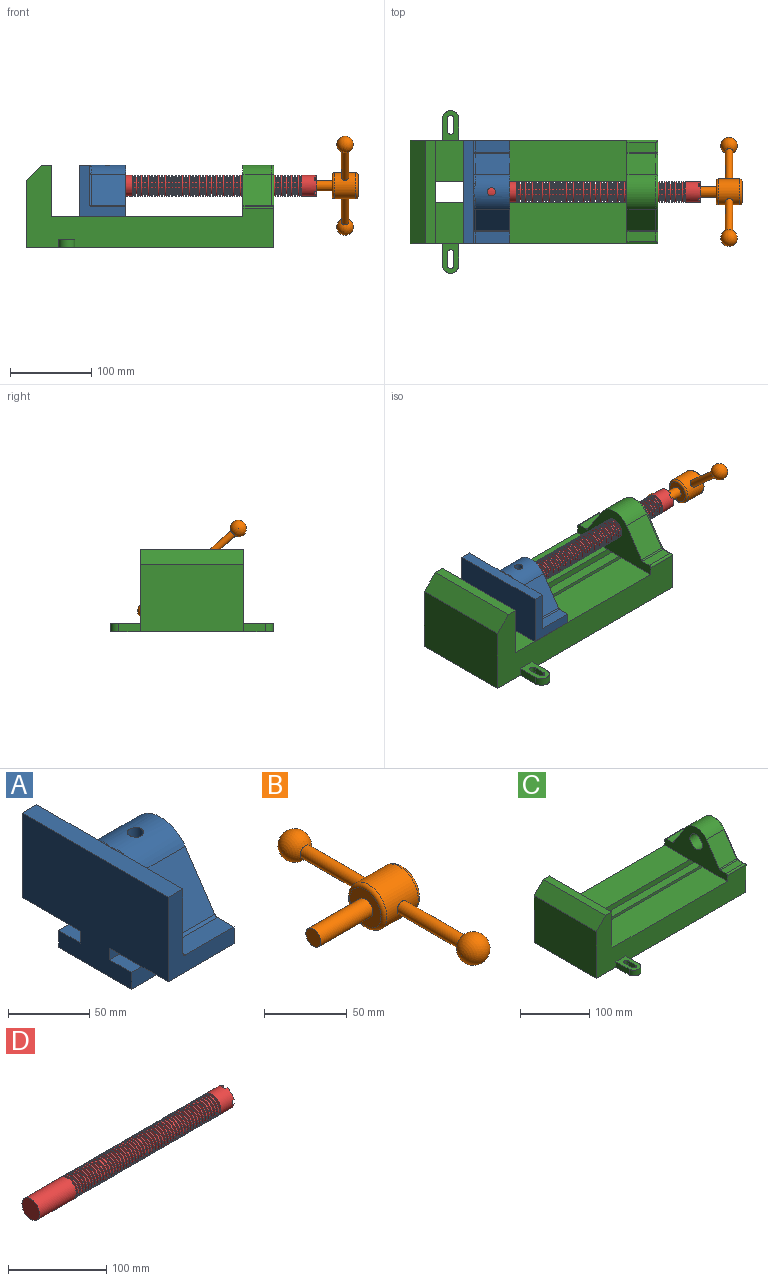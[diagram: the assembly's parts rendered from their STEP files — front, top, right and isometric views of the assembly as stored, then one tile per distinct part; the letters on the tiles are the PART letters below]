
ASSEMBLY  parts=4 mates=3
PART A: 36 faces, bbox 57.2x127x89 mm
  f0: plane 57.15x50.8mm, normal (0,0,-1), area 2903.2mm2, adj f6,f9,f10,f23
  f1: cylinder r=12.7mm len=44.45mm, axis (1,0,0), area 3464.3mm2, adj f6,f15,f16
  f2: plane 41.91x14.52mm, normal (0,0,1), area 608.5mm2, adj f6,f11,f24,f25
  f3: plane 51.86x48.26mm, normal (1,0,0), area 1495.7mm2, adj f8,f10,f31,f33,f35
  f4: plane 51.86x48.26mm, normal (1,0,0), area 1495.7mm2, adj f8,f11,f24,f28,f29
  f5: plane 57.15x50.8mm, normal (0,0,-1), area 2903.2mm2, adj f6,f9,f11,f22
  f6: plane 127x85.09mm, normal (1,0,0), area 5190.6mm2, adj f0,f1,f2,f5,f7,f10,f11,f12
  f7: plane 41.91x14.52mm, normal (0,0,1), area 608.5mm2, adj f6,f10,f30,f31
  f8: plane 127x12.7mm, normal (0,0,1), area 1612.9mm2, adj f3,f4,f9,f10,f11,f26,f34
  f9: plane 127x85.09mm, normal (-1,0,0), area 9096.8mm2, adj f0,f5,f8,f10,f11,f17,f18,f19
  f10: plane 63.5x57.15mm, normal (0,-1,0), area 1372.3mm2, adj f0,f3,f6,f7,f8,f9,f31
  f11: plane 63.5x57.15mm, normal (0,1,0), area 1372.3mm2, adj f2,f4,f5,f6,f8,f9,f24
  f12: plane 41.91x38.43mm, normal (0,-0.83,0.56), area 1939.2mm2, adj f6,f13,f30,f33
  f13: cylinder r=25.4mm len=44.45mm, axis (1,0,0), area 2026.5mm2, adj f6,f12,f14,f16,f26,f28,f34,f35
  f14: plane 41.91x38.43mm, normal (0,0.83,0.56), area 1939.2mm2, adj f6,f13,f25,f29
  f15: plane 25.4x25.4mm, normal (1,0,0), area 506.7mm2, adj f1
  f16: cylinder r=5.08mm len=13.76mm, axis (0,0,1), area 414mm2, adj f1,f13
  f17: plane 57.15x19.05mm, normal (0,0,1), area 1088.7mm2, adj f6,f9,f18,f23
  f18: plane 57.15x12.7mm, normal (0,-1,0), area 725.8mm2, adj f6,f9,f17,f19
  f19: plane 63.5x57.15mm, normal (0,0,-1), area 3629mm2, adj f6,f9,f18,f20
  f20: plane 57.15x12.7mm, normal (0,1,0), area 725.8mm2, adj f6,f9,f19,f21
  f21: plane 57.15x19.05mm, normal (0,0,1), area 1088.7mm2, adj f6,f9,f20,f22
  f22: plane 57.15x8.89mm, normal (0,1,0), area 508.1mm2, adj f5,f6,f9,f21
  f23: plane 57.15x8.89mm, normal (0,-1,0), area 508.1mm2, adj f0,f6,f9,f17
  f24: cylinder r=2.54mm len=14.52mm, axis (0,-1,0), area 57.9mm2, adj f2,f4,f11,f27
  f25: cylinder r=2.54mm len=41.91mm, axis (1,0,0), area 104.3mm2, adj f2,f6,f14,f27
  f26: bspline ~12.24x2.8mm, area 20.9mm2, adj f8,f13,f28
  f27: sphere r=2.54mm, area 6.3mm2, adj f24,f25,f29
  f28: torus R=27.94mm, axis (1,0,0), area 57.8mm2, adj f4,f13,f26,f29
  f29: cylinder r=2.54mm len=39.84mm, axis (0,-0.56,0.83), area 184.6mm2, adj f4,f14,f27,f28
  f30: cylinder r=2.54mm len=41.91mm, axis (1,0,0), area 104.3mm2, adj f6,f7,f12,f32
  f31: cylinder r=2.54mm len=14.52mm, axis (0,-1,0), area 57.9mm2, adj f3,f7,f10,f32
  f32: sphere r=2.54mm, area 6.3mm2, adj f30,f31,f33
  f33: cylinder r=2.54mm len=39.84mm, axis (0,-0.56,-0.83), area 184.6mm2, adj f3,f12,f32,f35
  f34: bspline ~12.24x2.8mm, area 20.9mm2, adj f8,f13,f35
  f35: torus R=27.94mm, axis (1,0,0), area 57.8mm2, adj f3,f13,f33,f34
PART B: 11 faces, bbox 76.2x172.7x34.4 mm
  f0: sphere r=10.16mm, area 1231.8mm2, adj f1
  f1: cylinder r=4.45mm len=51.82mm, axis (0,1,0), area 1438.5mm2, adj f0,f4
  f2: sphere r=10.16mm, area 1231.8mm2, adj f3
  f3: cylinder r=4.45mm len=51.82mm, axis (0,1,0), area 1438.5mm2, adj f2,f4
  f4: cylinder r=15.88mm len=31.75mm, axis (-1,0,0), area 2534.7mm2, adj f1,f3,f9,f10
  f5: cylinder r=6.35mm len=44.45mm, axis (-1,0,0), area 1773.5mm2, adj f6,f8
  f6: plane 12.7x12.7mm, normal (-1,0,0), area 126.7mm2, adj f5
  f7: plane 26.67x26.67mm, normal (1,0,0), area 558.6mm2, adj f10
  f8: plane 26.67x26.67mm, normal (-1,0,0), area 432mm2, adj f5,f9
  f9: torus R=13.33mm, axis (1,0,0), area 374.8mm2, adj f4,f8
  f10: torus R=13.33mm, axis (1,0,0), area 374.8mm2, adj f4,f7
PART C: 63 faces, bbox 305.3x200.5x106.7 mm
  f0: plane 305.34x200.54mm, normal (0,0,-1), area 32660.2mm2, adj f2,f4,f6,f9,f10,f22,f23,f40
  f1: plane 36.5x20mm, normal (0,0,1), area 516.8mm2, adj f2,f40,f41,f42,f43,f44,f45,f46
  f2: plane 304.8x101.6mm, normal (0,-1,0), area 13634.6mm2, adj f0,f1,f3,f4,f6,f7,f8,f9
  f3: plane 234.95x50.8mm, normal (0,0,1), area 11935.5mm2, adj f2,f6,f17,f27
  f4: plane 127x99.06mm, normal (1,0,0), area 7097.5mm2, adj f0,f2,f10,f15,f18,f19,f20,f21
  f5: plane 234.95x50.8mm, normal (0,0,1), area 11935.5mm2, adj f6,f10,f17,f28
  f6: plane 127x101.6mm, normal (1,0,0), area 9516.1mm2, adj f0,f2,f3,f5,f7,f10,f19,f20
  f7: plane 127x12.7mm, normal (0,0,1), area 1612.9mm2, adj f2,f6,f8,f10
  f8: plane 127x19.05mm, normal (-0.71,0,0.71), area 3421.5mm2, adj f2,f7,f9,f10
  f9: plane 127x82.55mm, normal (-1,0,0), area 10483.8mm2, adj f0,f2,f8,f10
  f10: plane 304.8x101.6mm, normal (0,1,0), area 13634.6mm2, adj f0,f4,f5,f6,f7,f8,f9,f17
  f11: plane 35.56x11.98mm, normal (0,0,1), area 426mm2, adj f17,f29,f30,f31
  f12: plane 38.43x35.56mm, normal (0,0.83,0.56), area 1645.4mm2, adj f13,f17,f30,f33
  f13: cylinder r=25.4mm len=42.19mm, axis (1,0,0), area 1770.2mm2, adj f12,f14,f17,f34
  f14: plane 38.43x35.56mm, normal (0,-0.83,0.56), area 1645.4mm2, adj f13,f17,f35,f36
  f15: cylinder r=12.7mm len=38.1mm, axis (1,0,0), area 3040.2mm2, adj f4,f17
  f16: plane 35.56x11.98mm, normal (0,0,1), area 426mm2, adj f17,f35,f37,f39
  f17: plane 127x63.5mm, normal (-1,0,0), area 4155.5mm2, adj f2,f3,f5,f10,f11,f12,f13,f14
  f18: plane 38.1x25.4mm, normal (0,0,-1), area 967.7mm2, adj f4,f17,f27,f28
  f19: plane 273.05x19.05mm, normal (0,0,-1), area 5201.6mm2, adj f4,f6,f20,f27
  f20: plane 273.05x12.7mm, normal (0,1,0), area 3467.7mm2, adj f4,f6,f19,f21
  f21: plane 273.05x19.05mm, normal (0,0,1), area 5201.6mm2, adj f4,f6,f20,f22
  f22: plane 273.05x16.51mm, normal (0,1,0), area 4508.1mm2, adj f0,f4,f6,f21
  f23: plane 273.05x16.51mm, normal (0,-1,0), area 4508.1mm2, adj f0,f4,f6,f24
  f24: plane 273.05x19.05mm, normal (0,0,1), area 5201.6mm2, adj f4,f6,f23,f25
  f25: plane 273.05x12.7mm, normal (0,-1,0), area 3467.7mm2, adj f4,f6,f24,f26
  f26: plane 273.05x19.05mm, normal (0,0,-1), area 5201.6mm2, adj f4,f6,f25,f28
  f27: plane 273.05x8.89mm, normal (0,1,0), area 2427.4mm2, adj f3,f4,f6,f18,f19
  f28: plane 273.05x8.89mm, normal (0,-1,0), area 2427.4mm2, adj f4,f5,f6,f18,f26
  f29: cylinder r=2.54mm len=38.1mm, axis (1,0,0), area 148.3mm2, adj f10,f11,f17,f31
  f30: cylinder r=2.54mm len=35.56mm, axis (-1,0,0), area 88.5mm2, adj f11,f12,f17,f32
  f31: cylinder r=2.54mm len=14.52mm, axis (0,1,0), area 54.3mm2, adj f4,f11,f29,f32
  f32: torus R=5.08mm, axis (-1,0,0), area 13.5mm2, adj f4,f30,f31,f33
  f33: cylinder r=2.54mm len=39.84mm, axis (0,0.56,-0.83), area 184.6mm2, adj f4,f12,f32,f34
  f34: torus R=22.86mm, axis (-1,0,0), area 191.4mm2, adj f4,f13,f33,f36
  f35: cylinder r=2.54mm len=35.56mm, axis (-1,0,0), area 88.5mm2, adj f14,f16,f17,f38
  f36: cylinder r=2.54mm len=39.84mm, axis (0,0.56,0.83), area 184.6mm2, adj f4,f14,f34,f38
  f37: cylinder r=2.54mm len=38.1mm, axis (-1,0,0), area 148.3mm2, adj f2,f16,f17,f39
  f38: torus R=5.08mm, axis (-1,0,0), area 13.5mm2, adj f4,f35,f36,f39
  f39: cylinder r=2.54mm len=14.52mm, axis (0,1,0), area 54.3mm2, adj f4,f16,f37,f38
  f40: plane 26.5x10mm, normal (-1,0,0), area 265mm2, adj f0,f1,f2,f42
  f41: plane 26.5x10mm, normal (1,0,0), area 265mm2, adj f0,f1,f2,f42
  f42: cylinder r=10mm len=20mm, axis (0,0,-1), area 314.2mm2, adj f0,f1,f40,f41
  f43: cylinder r=4mm len=10mm, axis (0,0,1), area 125.7mm2, adj f0,f1,f44,f46
  f44: plane 15x10mm, normal (-1,0,0), area 150mm2, adj f0,f1,f43,f45
  f45: cylinder r=4mm len=10mm, axis (0,0,1), area 125.7mm2, adj f0,f1,f44,f46
  f46: plane 15x10mm, normal (1,0,0), area 150mm2, adj f0,f1,f43,f45
  f47: plane 36.5x20mm, normal (0,0,1), area 516.8mm2, adj f10,f48,f49,f50,f51,f52,f53,f54
  f48: plane 26.5x10mm, normal (-1,0,0), area 265mm2, adj f0,f10,f47,f49
  f49: cylinder r=10mm len=20mm, axis (0,0,-1), area 314.2mm2, adj f0,f47,f48,f50
  f50: plane 26.5x10mm, normal (1,0,0), area 265mm2, adj f0,f10,f47,f49
  f51: cylinder r=4mm len=10mm, axis (0,0,1), area 125.7mm2, adj f0,f47,f52,f54
  f52: plane 15x10mm, normal (1,0,0), area 150mm2, adj f0,f47,f51,f53
  f53: cylinder r=4mm len=10mm, axis (0,0,1), area 125.7mm2, adj f0,f47,f52,f54
  f54: plane 15x10mm, normal (-1,0,0), area 150mm2, adj f0,f47,f51,f53
  f55: cylinder r=4.76mm len=11.35mm, axis (0,0.26,0.97), area 210.5mm2, adj f0,f56
  f56: plane 9.53x9.2mm, normal (0,-0.26,-0.97), area 58.9mm2, adj f55,f58
  f57: plane 3.97x3.83mm, normal (0,-0.26,-0.97), area 12.4mm2, adj f58
  f58: cylinder r=1.98mm len=13.29mm, axis (0,0.26,0.97), area 158.3mm2, adj f56,f57
  f59: cylinder r=4.76mm len=11.35mm, axis (0,0.26,0.97), area 210.5mm2, adj f0,f60
  f60: plane 9.53x9.2mm, normal (0,-0.26,-0.97), area 58.9mm2, adj f59,f62
  f61: plane 3.97x3.83mm, normal (0,-0.26,-0.97), area 12.4mm2, adj f62
  f62: cylinder r=1.98mm len=13.29mm, axis (0,0.26,0.97), area 158.3mm2, adj f60,f61
PART D: 220 faces, bbox 279.4x25.4x25.4 mm
  f0: cylinder r=12.7mm len=25.4mm, axis (-1,0,0), area 1468.2mm2, adj f1,f2,f3,f5,f7,f208,f209,f210
  f1: plane 9.9x9.9mm, normal (1,0,0), area 62.3mm2, adj f0,f4,f213,f216
  f2: plane 9.9x9.9mm, normal (1,0,0), area 62.3mm2, adj f0,f4,f210,f218
  f3: plane 9.9x9.9mm, normal (1,0,0), area 62.3mm2, adj f0,f4,f209,f212
  f4: cylinder r=6.35mm len=25.4mm, axis (1,0,0), area 960.3mm2, adj f1,f2,f3,f5,f6,f208,f209,f210
  f5: plane 9.9x9.9mm, normal (1,0,0), area 62.3mm2, adj f0,f4,f215,f217
  f6: plane 12.7x12.7mm, normal (1,0,0), area 126.7mm2, adj f4
  f7: cone r=12.7mm half-angle=76deg, axis (1,0,0), area 188mm2, adj f0,f9
  f8: cone r=10.16mm half-angle=76deg, axis (-1,0,0), area 188mm2, adj f9,f10
  f9: cylinder r=10.16mm len=20.32mm, axis (1,0,0), area 81.1mm2, adj f7,f8
  f10: cylinder r=12.7mm len=25.4mm, axis (-1,0,0), area 131.7mm2, adj f8,f11
  f11: cone r=12.7mm half-angle=76deg, axis (1,0,0), area 188mm2, adj f10,f13
  f12: cone r=10.16mm half-angle=76deg, axis (-1,0,0), area 188mm2, adj f13,f14
  f13: cylinder r=10.16mm len=20.32mm, axis (1,0,0), area 81.1mm2, adj f11,f12
  f14: cylinder r=12.7mm len=25.4mm, axis (-1,0,0), area 131.7mm2, adj f12,f15
  f15: cone r=12.7mm half-angle=76deg, axis (1,0,0), area 188mm2, adj f14,f17
  f16: cone r=10.16mm half-angle=76deg, axis (-1,0,0), area 188mm2, adj f17,f18
  f17: cylinder r=10.16mm len=20.32mm, axis (1,0,0), area 81.1mm2, adj f15,f16
  f18: cylinder r=12.7mm len=25.4mm, axis (-1,0,0), area 131.7mm2, adj f16,f19
  f19: cone r=12.7mm half-angle=76deg, axis (1,0,0), area 188mm2, adj f18,f21
  f20: cone r=10.16mm half-angle=76deg, axis (-1,0,0), area 188mm2, adj f21,f22
  f21: cylinder r=10.16mm len=20.32mm, axis (1,0,0), area 81.1mm2, adj f19,f20
  f22: cylinder r=12.7mm len=25.4mm, axis (-1,0,0), area 131.7mm2, adj f20,f23
  f23: cone r=12.7mm half-angle=76deg, axis (1,0,0), area 188mm2, adj f22,f25
  f24: cone r=10.16mm half-angle=76deg, axis (-1,0,0), area 188mm2, adj f25,f26
  f25: cylinder r=10.16mm len=20.32mm, axis (1,0,0), area 81.1mm2, adj f23,f24
  f26: cylinder r=12.7mm len=25.4mm, axis (-1,0,0), area 131.7mm2, adj f24,f27
  f27: cone r=12.7mm half-angle=76deg, axis (1,0,0), area 188mm2, adj f26,f29
  f28: cone r=10.16mm half-angle=76deg, axis (-1,0,0), area 188mm2, adj f29,f30
  f29: cylinder r=10.16mm len=20.32mm, axis (1,0,0), area 81.1mm2, adj f27,f28
  f30: cylinder r=12.7mm len=25.4mm, axis (-1,0,0), area 131.7mm2, adj f28,f31
  f31: cone r=12.7mm half-angle=76deg, axis (1,0,0), area 188mm2, adj f30,f33
  f32: cone r=10.16mm half-angle=76deg, axis (-1,0,0), area 188mm2, adj f33,f34
  f33: cylinder r=10.16mm len=20.32mm, axis (1,0,0), area 81.1mm2, adj f31,f32
  f34: cylinder r=12.7mm len=25.4mm, axis (-1,0,0), area 131.7mm2, adj f32,f35
  f35: cone r=12.7mm half-angle=76deg, axis (1,0,0), area 188mm2, adj f34,f37
  f36: cone r=10.16mm half-angle=76deg, axis (-1,0,0), area 188mm2, adj f37,f38
  f37: cylinder r=10.16mm len=20.32mm, axis (1,0,0), area 81.1mm2, adj f35,f36
  f38: cylinder r=12.7mm len=25.4mm, axis (-1,0,0), area 131.7mm2, adj f36,f39
  f39: cone r=12.7mm half-angle=76deg, axis (1,0,0), area 188mm2, adj f38,f41
  f40: cone r=10.16mm half-angle=76deg, axis (-1,0,0), area 188mm2, adj f41,f42
  f41: cylinder r=10.16mm len=20.32mm, axis (1,0,0), area 81.1mm2, adj f39,f40
  f42: cylinder r=12.7mm len=25.4mm, axis (-1,0,0), area 131.7mm2, adj f40,f43
  f43: cone r=12.7mm half-angle=76deg, axis (1,0,0), area 188mm2, adj f42,f45
  f44: cone r=10.16mm half-angle=76deg, axis (-1,0,0), area 188mm2, adj f45,f46
  f45: cylinder r=10.16mm len=20.32mm, axis (1,0,0), area 81.1mm2, adj f43,f44
  f46: cylinder r=12.7mm len=25.4mm, axis (-1,0,0), area 131.7mm2, adj f44,f47
  f47: cone r=12.7mm half-angle=76deg, axis (1,0,0), area 188mm2, adj f46,f49
  f48: cone r=10.16mm half-angle=76deg, axis (-1,0,0), area 188mm2, adj f49,f50
  f49: cylinder r=10.16mm len=20.32mm, axis (1,0,0), area 81.1mm2, adj f47,f48
  f50: cylinder r=12.7mm len=25.4mm, axis (-1,0,0), area 131.7mm2, adj f48,f51
  f51: cone r=12.7mm half-angle=76deg, axis (1,0,0), area 188mm2, adj f50,f53
  f52: cone r=10.16mm half-angle=76deg, axis (-1,0,0), area 188mm2, adj f53,f54
  f53: cylinder r=10.16mm len=20.32mm, axis (1,0,0), area 81.1mm2, adj f51,f52
  f54: cylinder r=12.7mm len=25.4mm, axis (-1,0,0), area 131.7mm2, adj f52,f55
  f55: cone r=12.7mm half-angle=76deg, axis (1,0,0), area 188mm2, adj f54,f57
  f56: cone r=10.16mm half-angle=76deg, axis (-1,0,0), area 188mm2, adj f57,f58
  f57: cylinder r=10.16mm len=20.32mm, axis (1,0,0), area 81.1mm2, adj f55,f56
  f58: cylinder r=12.7mm len=25.4mm, axis (-1,0,0), area 131.7mm2, adj f56,f59
  f59: cone r=12.7mm half-angle=76deg, axis (1,0,0), area 188mm2, adj f58,f61
  f60: cone r=10.16mm half-angle=76deg, axis (-1,0,0), area 188mm2, adj f61,f62
  f61: cylinder r=10.16mm len=20.32mm, axis (1,0,0), area 81.1mm2, adj f59,f60
  f62: cylinder r=12.7mm len=25.4mm, axis (-1,0,0), area 131.7mm2, adj f60,f63
  f63: cone r=12.7mm half-angle=76deg, axis (1,0,0), area 188mm2, adj f62,f65
  f64: cone r=10.16mm half-angle=76deg, axis (-1,0,0), area 188mm2, adj f65,f66
  f65: cylinder r=10.16mm len=20.32mm, axis (1,0,0), area 81.1mm2, adj f63,f64
  f66: cylinder r=12.7mm len=25.4mm, axis (-1,0,0), area 131.7mm2, adj f64,f67
  f67: cone r=12.7mm half-angle=76deg, axis (1,0,0), area 188mm2, adj f66,f69
  f68: cone r=10.16mm half-angle=76deg, axis (-1,0,0), area 188mm2, adj f69,f70
  f69: cylinder r=10.16mm len=20.32mm, axis (1,0,0), area 81.1mm2, adj f67,f68
  f70: cylinder r=12.7mm len=25.4mm, axis (-1,0,0), area 131.7mm2, adj f68,f71
  f71: cone r=12.7mm half-angle=76deg, axis (1,0,0), area 188mm2, adj f70,f73
  f72: cone r=10.16mm half-angle=76deg, axis (-1,0,0), area 188mm2, adj f73,f74
  f73: cylinder r=10.16mm len=20.32mm, axis (1,0,0), area 81.1mm2, adj f71,f72
  f74: cylinder r=12.7mm len=25.4mm, axis (-1,0,0), area 131.7mm2, adj f72,f75
  f75: cone r=12.7mm half-angle=76deg, axis (1,0,0), area 188mm2, adj f74,f77
  f76: cone r=10.16mm half-angle=76deg, axis (-1,0,0), area 188mm2, adj f77,f78
  f77: cylinder r=10.16mm len=20.32mm, axis (1,0,0), area 81.1mm2, adj f75,f76
  f78: cylinder r=12.7mm len=25.4mm, axis (-1,0,0), area 131.7mm2, adj f76,f79
  f79: cone r=12.7mm half-angle=76deg, axis (1,0,0), area 188mm2, adj f78,f81
  f80: cone r=10.16mm half-angle=76deg, axis (-1,0,0), area 188mm2, adj f81,f82
  f81: cylinder r=10.16mm len=20.32mm, axis (1,0,0), area 81.1mm2, adj f79,f80
  f82: cylinder r=12.7mm len=25.4mm, axis (-1,0,0), area 131.7mm2, adj f80,f83
  f83: cone r=12.7mm half-angle=76deg, axis (1,0,0), area 188mm2, adj f82,f85
  f84: cone r=10.16mm half-angle=76deg, axis (-1,0,0), area 188mm2, adj f85,f86
  f85: cylinder r=10.16mm len=20.32mm, axis (1,0,0), area 81.1mm2, adj f83,f84
  f86: cylinder r=12.7mm len=25.4mm, axis (-1,0,0), area 131.7mm2, adj f84,f87
  f87: cone r=12.7mm half-angle=76deg, axis (1,0,0), area 188mm2, adj f86,f89
  f88: cone r=10.16mm half-angle=76deg, axis (-1,0,0), area 188mm2, adj f89,f90
  f89: cylinder r=10.16mm len=20.32mm, axis (1,0,0), area 81.1mm2, adj f87,f88
  f90: cylinder r=12.7mm len=25.4mm, axis (-1,0,0), area 131.7mm2, adj f88,f91
  f91: cone r=12.7mm half-angle=76deg, axis (1,0,0), area 188mm2, adj f90,f93
  f92: cone r=10.16mm half-angle=76deg, axis (-1,0,0), area 188mm2, adj f93,f94
  f93: cylinder r=10.16mm len=20.32mm, axis (1,0,0), area 81.1mm2, adj f91,f92
  f94: cylinder r=12.7mm len=25.4mm, axis (-1,0,0), area 131.7mm2, adj f92,f95
  f95: cone r=12.7mm half-angle=76deg, axis (1,0,0), area 188mm2, adj f94,f97
  f96: cone r=10.16mm half-angle=76deg, axis (-1,0,0), area 188mm2, adj f97,f98
  f97: cylinder r=10.16mm len=20.32mm, axis (1,0,0), area 81.1mm2, adj f95,f96
  f98: cylinder r=12.7mm len=25.4mm, axis (-1,0,0), area 131.7mm2, adj f96,f99
  f99: cone r=12.7mm half-angle=76deg, axis (1,0,0), area 188mm2, adj f98,f101
  f100: cone r=10.16mm half-angle=76deg, axis (-1,0,0), area 188mm2, adj f101,f102
  f101: cylinder r=10.16mm len=20.32mm, axis (1,0,0), area 81.1mm2, adj f99,f100
  f102: cylinder r=12.7mm len=25.4mm, axis (-1,0,0), area 131.7mm2, adj f100,f103
  f103: cone r=12.7mm half-angle=76deg, axis (1,0,0), area 188mm2, adj f102,f105
  f104: cone r=10.16mm half-angle=76deg, axis (-1,0,0), area 188mm2, adj f105,f106
  f105: cylinder r=10.16mm len=20.32mm, axis (1,0,0), area 81.1mm2, adj f103,f104
  f106: cylinder r=12.7mm len=25.4mm, axis (-1,0,0), area 131.7mm2, adj f104,f107
  f107: cone r=12.7mm half-angle=76deg, axis (1,0,0), area 188mm2, adj f106,f109
  f108: cone r=10.16mm half-angle=76deg, axis (-1,0,0), area 188mm2, adj f109,f110
  f109: cylinder r=10.16mm len=20.32mm, axis (1,0,0), area 81.1mm2, adj f107,f108
  f110: cylinder r=12.7mm len=25.4mm, axis (-1,0,0), area 131.7mm2, adj f108,f111
  f111: cone r=12.7mm half-angle=76deg, axis (1,0,0), area 188mm2, adj f110,f113
  f112: cone r=10.16mm half-angle=76deg, axis (-1,0,0), area 188mm2, adj f113,f114
  f113: cylinder r=10.16mm len=20.32mm, axis (1,0,0), area 81.1mm2, adj f111,f112
  f114: cylinder r=12.7mm len=25.4mm, axis (-1,0,0), area 131.7mm2, adj f112,f115
  f115: cone r=12.7mm half-angle=76deg, axis (1,0,0), area 188mm2, adj f114,f117
  f116: cone r=10.16mm half-angle=76deg, axis (-1,0,0), area 188mm2, adj f117,f118
  f117: cylinder r=10.16mm len=20.32mm, axis (1,0,0), area 81.1mm2, adj f115,f116
  f118: cylinder r=12.7mm len=25.4mm, axis (-1,0,0), area 131.7mm2, adj f116,f119
  f119: cone r=12.7mm half-angle=76deg, axis (1,0,0), area 188mm2, adj f118,f121
  f120: cone r=10.16mm half-angle=76deg, axis (-1,0,0), area 188mm2, adj f121,f122
  f121: cylinder r=10.16mm len=20.32mm, axis (1,0,0), area 81.1mm2, adj f119,f120
  f122: cylinder r=12.7mm len=25.4mm, axis (-1,0,0), area 131.7mm2, adj f120,f123
  f123: cone r=12.7mm half-angle=76deg, axis (1,0,0), area 188mm2, adj f122,f125
  f124: cone r=10.16mm half-angle=76deg, axis (-1,0,0), area 188mm2, adj f125,f126
  f125: cylinder r=10.16mm len=20.32mm, axis (1,0,0), area 81.1mm2, adj f123,f124
  f126: cylinder r=12.7mm len=25.4mm, axis (-1,0,0), area 131.7mm2, adj f124,f127
  f127: cone r=12.7mm half-angle=76deg, axis (1,0,0), area 188mm2, adj f126,f129
  f128: cone r=10.16mm half-angle=76deg, axis (-1,0,0), area 188mm2, adj f129,f130
  f129: cylinder r=10.16mm len=20.32mm, axis (1,0,0), area 81.1mm2, adj f127,f128
  f130: cylinder r=12.7mm len=25.4mm, axis (-1,0,0), area 131.7mm2, adj f128,f131
  f131: cone r=12.7mm half-angle=76deg, axis (1,0,0), area 188mm2, adj f130,f133
  f132: cone r=10.16mm half-angle=76deg, axis (-1,0,0), area 188mm2, adj f133,f134
  f133: cylinder r=10.16mm len=20.32mm, axis (1,0,0), area 81.1mm2, adj f131,f132
  f134: cylinder r=12.7mm len=25.4mm, axis (-1,0,0), area 131.7mm2, adj f132,f135
  f135: cone r=12.7mm half-angle=76deg, axis (1,0,0), area 188mm2, adj f134,f137
  f136: cone r=10.16mm half-angle=76deg, axis (-1,0,0), area 188mm2, adj f137,f138
  f137: cylinder r=10.16mm len=20.32mm, axis (1,0,0), area 81.1mm2, adj f135,f136
  f138: cylinder r=12.7mm len=25.4mm, axis (-1,0,0), area 131.7mm2, adj f136,f139
  f139: cone r=12.7mm half-angle=76deg, axis (1,0,0), area 188mm2, adj f138,f141
  f140: cone r=10.16mm half-angle=76deg, axis (-1,0,0), area 188mm2, adj f141,f142
  f141: cylinder r=10.16mm len=20.32mm, axis (1,0,0), area 81.1mm2, adj f139,f140
  f142: cylinder r=12.7mm len=25.4mm, axis (-1,0,0), area 131.7mm2, adj f140,f143
  f143: cone r=12.7mm half-angle=76deg, axis (1,0,0), area 188mm2, adj f142,f145
  f144: cone r=10.16mm half-angle=76deg, axis (-1,0,0), area 188mm2, adj f145,f146
  f145: cylinder r=10.16mm len=20.32mm, axis (1,0,0), area 81.1mm2, adj f143,f144
  f146: cylinder r=12.7mm len=25.4mm, axis (-1,0,0), area 131.7mm2, adj f144,f147
  f147: cone r=12.7mm half-angle=76deg, axis (1,0,0), area 188mm2, adj f146,f149
  f148: cone r=10.16mm half-angle=76deg, axis (-1,0,0), area 188mm2, adj f149,f150
  f149: cylinder r=10.16mm len=20.32mm, axis (1,0,0), area 81.1mm2, adj f147,f148
  f150: cylinder r=12.7mm len=25.4mm, axis (-1,0,0), area 131.7mm2, adj f148,f151
  f151: cone r=12.7mm half-angle=76deg, axis (1,0,0), area 188mm2, adj f150,f153
  f152: cone r=10.16mm half-angle=76deg, axis (-1,0,0), area 188mm2, adj f153,f154
  f153: cylinder r=10.16mm len=20.32mm, axis (1,0,0), area 81.1mm2, adj f151,f152
  f154: cylinder r=12.7mm len=25.4mm, axis (-1,0,0), area 131.7mm2, adj f152,f155
  f155: cone r=12.7mm half-angle=76deg, axis (1,0,0), area 188mm2, adj f154,f157
  f156: cone r=10.16mm half-angle=76deg, axis (-1,0,0), area 188mm2, adj f157,f158
  f157: cylinder r=10.16mm len=20.32mm, axis (1,0,0), area 81.1mm2, adj f155,f156
  f158: cylinder r=12.7mm len=25.4mm, axis (-1,0,0), area 131.7mm2, adj f156,f159
  f159: cone r=12.7mm half-angle=76deg, axis (1,0,0), area 188mm2, adj f158,f161
  f160: cone r=10.16mm half-angle=76deg, axis (-1,0,0), area 188mm2, adj f161,f162
  f161: cylinder r=10.16mm len=20.32mm, axis (1,0,0), area 81.1mm2, adj f159,f160
  f162: cylinder r=12.7mm len=25.4mm, axis (-1,0,0), area 131.7mm2, adj f160,f163
  f163: cone r=12.7mm half-angle=76deg, axis (1,0,0), area 188mm2, adj f162,f165
  f164: cone r=10.16mm half-angle=76deg, axis (-1,0,0), area 188mm2, adj f165,f166
  f165: cylinder r=10.16mm len=20.32mm, axis (1,0,0), area 81.1mm2, adj f163,f164
  f166: cylinder r=12.7mm len=25.4mm, axis (-1,0,0), area 131.7mm2, adj f164,f167
  f167: cone r=12.7mm half-angle=76deg, axis (1,0,0), area 188mm2, adj f166,f169
  f168: cone r=10.16mm half-angle=76deg, axis (-1,0,0), area 188mm2, adj f169,f170
  f169: cylinder r=10.16mm len=20.32mm, axis (1,0,0), area 81.1mm2, adj f167,f168
  f170: cylinder r=12.7mm len=25.4mm, axis (-1,0,0), area 131.7mm2, adj f168,f171
  f171: cone r=12.7mm half-angle=76deg, axis (1,0,0), area 188mm2, adj f170,f173
  f172: cone r=10.16mm half-angle=76deg, axis (-1,0,0), area 188mm2, adj f173,f174
  f173: cylinder r=10.16mm len=20.32mm, axis (1,0,0), area 81.1mm2, adj f171,f172
  f174: cylinder r=12.7mm len=25.4mm, axis (-1,0,0), area 131.7mm2, adj f172,f175
  f175: cone r=12.7mm half-angle=76deg, axis (1,0,0), area 188mm2, adj f174,f177
  f176: cone r=10.16mm half-angle=76deg, axis (-1,0,0), area 188mm2, adj f177,f178
  f177: cylinder r=10.16mm len=20.32mm, axis (1,0,0), area 81.1mm2, adj f175,f176
  f178: cylinder r=12.7mm len=25.4mm, axis (-1,0,0), area 131.7mm2, adj f176,f179
  f179: cone r=12.7mm half-angle=76deg, axis (1,0,0), area 188mm2, adj f178,f181
  f180: cone r=10.16mm half-angle=76deg, axis (-1,0,0), area 188mm2, adj f181,f182
  f181: cylinder r=10.16mm len=20.32mm, axis (1,0,0), area 81.1mm2, adj f179,f180
  f182: cylinder r=12.7mm len=25.4mm, axis (-1,0,0), area 131.7mm2, adj f180,f183
  f183: cone r=12.7mm half-angle=76deg, axis (1,0,0), area 188mm2, adj f182,f185
  f184: cone r=10.16mm half-angle=76deg, axis (-1,0,0), area 188mm2, adj f185,f186
  f185: cylinder r=10.16mm len=20.32mm, axis (1,0,0), area 81.1mm2, adj f183,f184
  f186: cylinder r=12.7mm len=25.4mm, axis (-1,0,0), area 131.7mm2, adj f184,f187
  f187: cone r=12.7mm half-angle=76deg, axis (1,0,0), area 188mm2, adj f186,f189
  f188: cone r=10.16mm half-angle=76deg, axis (-1,0,0), area 188mm2, adj f189,f190
  f189: cylinder r=10.16mm len=20.32mm, axis (1,0,0), area 81.1mm2, adj f187,f188
  f190: cylinder r=12.7mm len=25.4mm, axis (-1,0,0), area 131.7mm2, adj f188,f191
  f191: cone r=12.7mm half-angle=76deg, axis (1,0,0), area 188mm2, adj f190,f193
  f192: cone r=10.16mm half-angle=76deg, axis (-1,0,0), area 188mm2, adj f193,f194
  f193: cylinder r=10.16mm len=20.32mm, axis (1,0,0), area 81.1mm2, adj f191,f192
  f194: cylinder r=12.7mm len=25.4mm, axis (-1,0,0), area 131.7mm2, adj f192,f195
  f195: cone r=12.7mm half-angle=76deg, axis (1,0,0), area 188mm2, adj f194,f197
  f196: cone r=10.16mm half-angle=76deg, axis (-1,0,0), area 188mm2, adj f197,f198
  f197: cylinder r=10.16mm len=20.32mm, axis (1,0,0), area 81.1mm2, adj f195,f196
  f198: cylinder r=12.7mm len=25.4mm, axis (-1,0,0), area 131.7mm2, adj f196,f199
  f199: cone r=12.7mm half-angle=76deg, axis (1,0,0), area 188mm2, adj f198,f201
  f200: cone r=10.16mm half-angle=76deg, axis (-1,0,0), area 188mm2, adj f201,f202
  f201: cylinder r=10.16mm len=20.32mm, axis (1,0,0), area 81.1mm2, adj f199,f200
  f202: cylinder r=12.7mm len=25.4mm, axis (-1,0,0), area 131.7mm2, adj f200,f203
  f203: cone r=12.7mm half-angle=76deg, axis (1,0,0), area 188mm2, adj f202,f205
  f204: cone r=10.16mm half-angle=76deg, axis (-1,0,0), area 188mm2, adj f205,f207
  f205: cylinder r=10.16mm len=20.32mm, axis (1,0,0), area 81.1mm2, adj f203,f204
  f206: plane 25.4x25.4mm, normal (-1,0,0), area 506.7mm2, adj f207
  f207: cylinder r=12.7mm len=52.45mm, axis (-1,0,0), area 4185.4mm2, adj f204,f206
  f208: plane 6.88x5.08mm, normal (1,0,0), area 32.7mm2, adj f0,f4,f209,f210
  f209: plane 6.62x2.54mm, normal (0,-1,0), area 16.8mm2, adj f0,f3,f4,f208
  f210: plane 6.62x2.54mm, normal (0,1,0), area 16.8mm2, adj f0,f2,f4,f208
  f211: plane 6.88x5.08mm, normal (1,0,0), area 32.7mm2, adj f0,f4,f212,f213
  f212: plane 6.62x2.54mm, normal (0,0,1), area 16.8mm2, adj f0,f3,f4,f211
  f213: plane 6.62x2.54mm, normal (0,0,-1), area 16.8mm2, adj f0,f1,f4,f211
  f214: plane 6.88x5.08mm, normal (1,0,0), area 32.7mm2, adj f0,f4,f215,f216
  f215: plane 6.62x2.54mm, normal (0,1,0), area 16.8mm2, adj f0,f4,f5,f214
  f216: plane 6.62x2.54mm, normal (0,-1,0), area 16.8mm2, adj f0,f1,f4,f214
  f217: plane 6.62x2.54mm, normal (0,0,-1), area 16.8mm2, adj f0,f4,f5,f219
  f218: plane 6.62x2.54mm, normal (0,0,1), area 16.8mm2, adj f0,f2,f4,f219
  f219: plane 6.88x5.08mm, normal (1,0,0), area 32.7mm2, adj f0,f4,f217,f218
PLACE A t=(33.48,0,0)mm
PLACE B rot(axis=(-1,0,0),41.7deg) t=(33.48,-50.69,19.31)mm
PLACE C at identity fixed
PLACE D rot(axis=(-1,0,0),41.7deg) t=(33.48,-50.69,19.31)mm
MATE revolute A.f28 <-> D.f7  axis (1,0,0) through (-226.87,0,76.2)mm
MATE fastened B.f5 <-> D.f4  axis (-1,0,0) through (27.13,0,76.2)mm
MATE slider A.f9 <-> C.f6  axis (-1,0,0) through (-239.57,-63.5,38.1)mm
